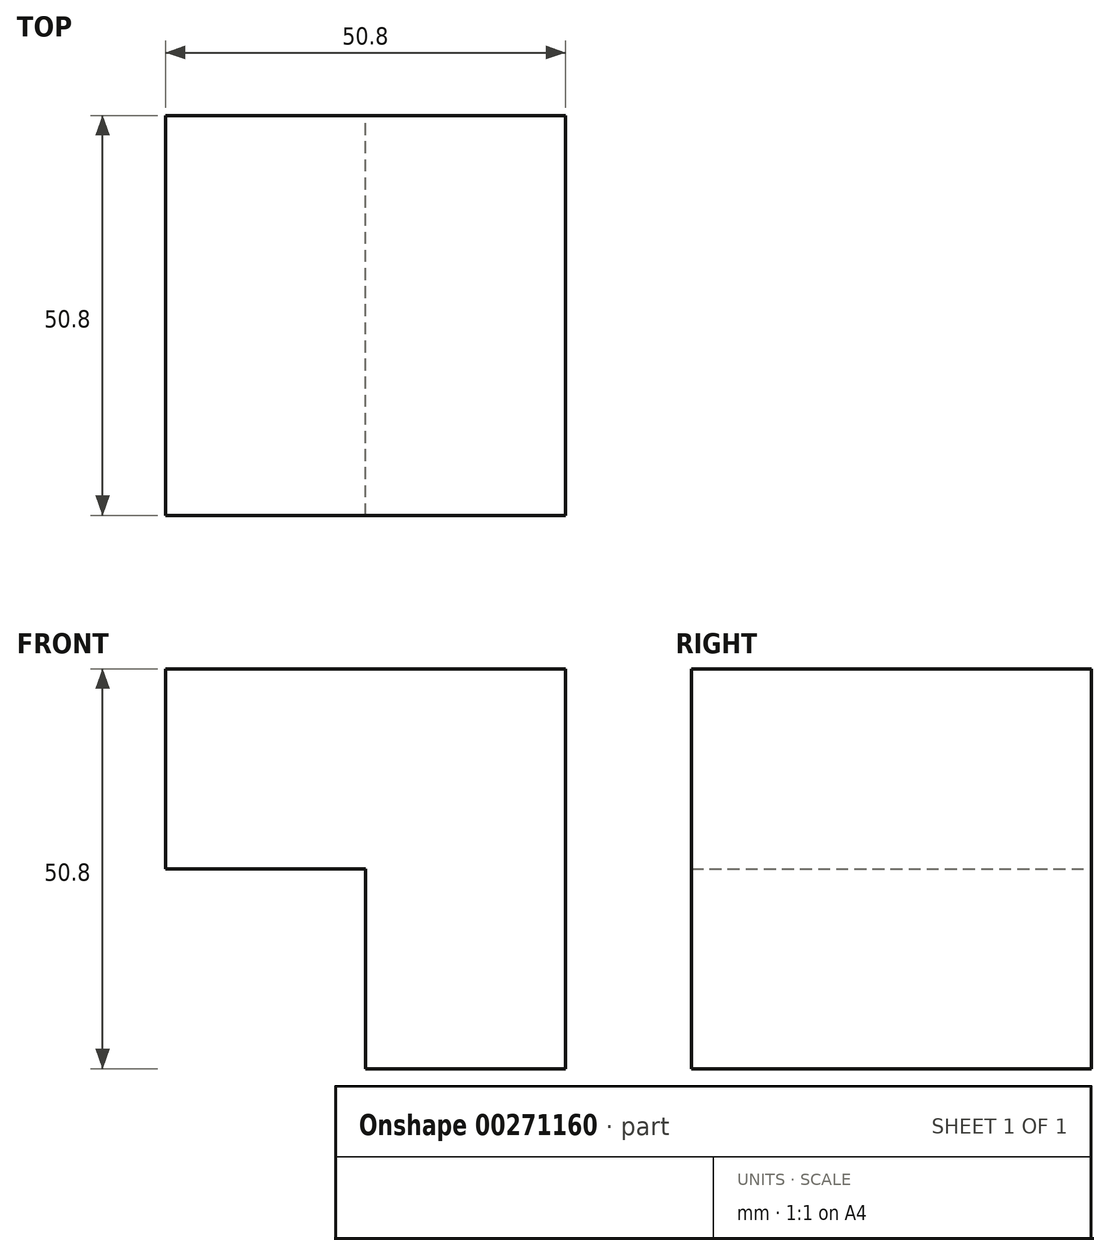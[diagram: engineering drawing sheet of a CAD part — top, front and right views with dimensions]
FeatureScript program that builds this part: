
annotation { "Feature Type Name" : "Feature", "Feature Type Description" : "" }
export const myFeature = defineFeature(function(context is Context, id is Id, definition is map)
    precondition{}
    {
        {
            var Q0;
            Q0=qCreatedBy(makeId("Front.planeOp"),FACE);
            var sketch = newSketch(context, id + "F0", { "sketchPlane" : qUnion([Q0])});
            skLineSegment(sketch, "E0", {"start": v(0, 0) * mm, "end": v(0, 50.8) * mm});
            skLineSegment(sketch, "E1", {"start": v(0, 50.8) * mm, "end": v(-50.8, 50.8) * mm});
            skLineSegment(sketch, "E2", {"start": v(-50.8, 50.8) * mm, "end": v(-50.8, 25.4) * mm});
            skLineSegment(sketch, "E3", {"start": v(-50.8, 25.4) * mm, "end": v(-25.4, 25.4) * mm});
            skLineSegment(sketch, "E4", {"start": v(-25.4, 25.4) * mm, "end": v(-25.4, 0) * mm});
            skLineSegment(sketch, "E5", {"start": v(0, 0) * mm, "end": v(-25.4, 0) * mm});
            skSolve(sketch);
        }
        {
            var Q0;
            Q0=makeQuery(id+"F0.imprint","IMPRINT",FACE,{"disambiguationData":[TD([[makeQuery(id+"F0.imprint","IMPRINT",EDGE,{"derivedFrom":sQuery(id+"F0.wireOp",EDGE,"E0")}),1.0]])]});
            extrude(context, id + "F1", {"entities" : qUnion([Q0]), "depth" : 50.8 * mm});
        }
    });
